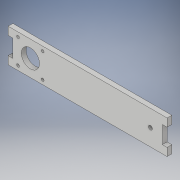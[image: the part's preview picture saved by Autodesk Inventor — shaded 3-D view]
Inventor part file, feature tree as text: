
AUTODESK INVENTOR PART (.ipt)
format: ipt  version: 2019 (Build 230136000, 136)  size: 133,632 bytes
history: native  units: mm
features: extrude x1, sketch x1
ambient origin geometry x8: Origin, YZ Plane, XZ Plane, XY Plane, X Axis, Y Axis, Z Axis, Center Point
bodies: Body1 (feature_tree)
feature tree (2):
  extrude  "Extrusion2"  Depth=21.0mm
  sketch  "Sketch1"  dims[d13=3.5mm d14=3.5mm d15=15.5mm d16=15.5mm d21=3.5mm d22=3.5mm d23=31.0mm d24=23.0mm d25=6.0mm d26=0.0mm d29=21.0mm d30=15.5mm d31=200.0mm d32=21.0mm d34=21.0mm d35=6.0mm d36=10.0mm d37=10.0mm d38=28.0mm d39=10.0mm d40=10.0mm d41=6.0mm d42=5.0mm d43=15.0mm d44=21.0mm]
